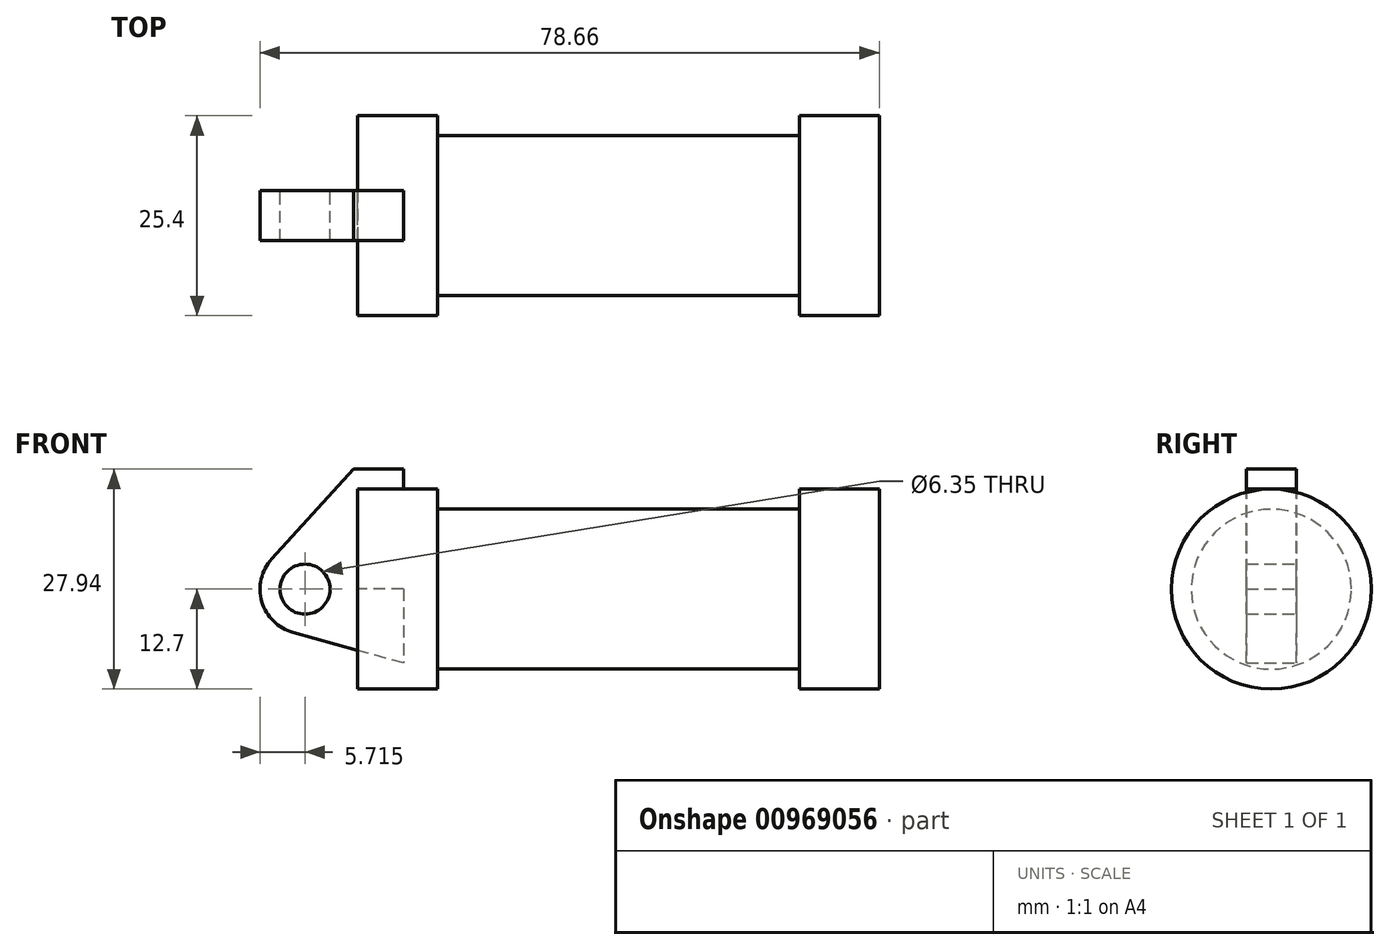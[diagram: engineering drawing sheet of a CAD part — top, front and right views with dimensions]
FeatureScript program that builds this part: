
annotation { "Feature Type Name" : "Feature", "Feature Type Description" : "" }
export const myFeature = defineFeature(function(context is Context, id is Id, definition is map)
    precondition{}
    {
        {
            var Q0;
            Q0=qCreatedBy(makeId("Front.planeOp"),FACE);
            var sketch = newSketch(context, id + "F0", { "sketchPlane" : qUnion([Q0])});
            skLineSegment(sketch, "E0", {"start": v(0, 0) * mm, "end": v(0, 12.7) * mm});
            skLineSegment(sketch, "E1", {"start": v(0, 12.7) * mm, "end": v(10.16, 12.7) * mm});
            skLineSegment(sketch, "E2", {"start": v(10.16, 12.7) * mm, "end": v(10.16, 10.16) * mm});
            skLineSegment(sketch, "E3", {"start": v(10.16, 10.16) * mm, "end": v(56.13, 10.16) * mm});
            skLineSegment(sketch, "E4", {"start": v(56.13, 10.16) * mm, "end": v(56.13, 12.7) * mm});
            skLineSegment(sketch, "E5", {"start": v(56.13, 12.7) * mm, "end": v(66.3, 12.7) * mm});
            skLineSegment(sketch, "E6", {"start": v(66.3, 12.7) * mm, "end": v(66.3, 0) * mm});
            skLineSegment(sketch, "E7", {"start": v(66.3, 0) * mm, "end": v(0, 0) * mm});
            skLineSegment(sketch, "E8", {"start": v(5.84, 15.24) * mm, "end": v(-0.5, 15.24) * mm});
            skLineSegment(sketch, "E9", {"start": v(-0.5, 15.24) * mm, "end": v(-10.88, 3.85) * mm});
            skLineSegment(sketch, "E10", {"start": v(0, 0) * mm, "end": v(-6.65, 0) * mm});
            skCircle(sketch, "E11", {"center": v(-6.65, 0) * mm, "radius": 5.72 * mm});
            skCircle(sketch, "E12", {"center": v(-6.65, 0) * mm, "radius": 3.18 * mm});
            skLineSegment(sketch, "E13", {"start": v(5.84, 15.24) * mm, "end": v(5.84, -9.4) * mm});
            skLineSegment(sketch, "E14", {"start": v(5.84, -9.4) * mm, "end": v(-8.18, -5.5) * mm});
            skSolve(sketch);
        }
        {
            var Q0;
            {var subQ0=sQuery(id+"F0.wireOp",EDGE,"E0");Q0=makeQuery(id+"F0.imprint","IMPRINT",FACE,{"disambiguationData":[TD([[makeQuery(id+"F0.imprint","IMPRINT",EDGE,{"derivedFrom":subQ0}),-1.0]])]});}
            var Q1;
            {var subQ0=sQuery(id+"F0.wireOp",EDGE,"E2");Q1=makeQuery(id+"F0.imprint","IMPRINT",FACE,{"disambiguationData":[TD([[makeQuery(id+"F0.imprint","IMPRINT",EDGE,{"derivedFrom":subQ0}),-1.0]])]});}
            var Q2;
            Q2=sQuery(id+"F0.wireOp",EDGE,"E7");
            revolve(context, id + "F1", {"surfaceOperationType" : NewSurfaceOperationType.NEW, "entities" : qUnion([Q0, Q1]), "axis" : qUnion([Q2]), "revolveType" : RevolveType.FULL});
        }
        {
            var Q0;
            {var subQ1=sQuery(id+"F0.wireOp",EDGE,"E0");Q0=makeQuery(id+"F0.imprint","IMPRINT",FACE,{"disambiguationData":[TD([[makeQuery(id+"F0.imprint","IMPRINT",EDGE,{"derivedFrom":subQ1}),1.0]])]});}
            var Q1;
            {var subQ5=sQuery(id+"F0.wireOp",EDGE,"E12");Q1=makeQuery(id+"F0.imprint","IMPRINT",FACE,{"disambiguationData":[TD([[makeQuery(id+"F0.imprint","IMPRINT",EDGE,{"derivedFrom":subQ5}),-1.0]])]});}
            var Q2;
            {var subQ0=sQuery(id+"F0.wireOp",EDGE,"E14");Q2=makeQuery(id+"F0.imprint","IMPRINT",FACE,{"disambiguationData":[TD([[makeQuery(id+"F0.imprint","IMPRINT",EDGE,{"derivedFrom":subQ0}),-1.0]])]});}
            extrude(context, id + "F2", {"entities" : qUnion([Q0, Q1, Q2]), "endBound" : BoundingType.SYMMETRIC, "depth" : 6.35 * mm, "offsetDistance" : 25.4 * mm});
        }
    });
